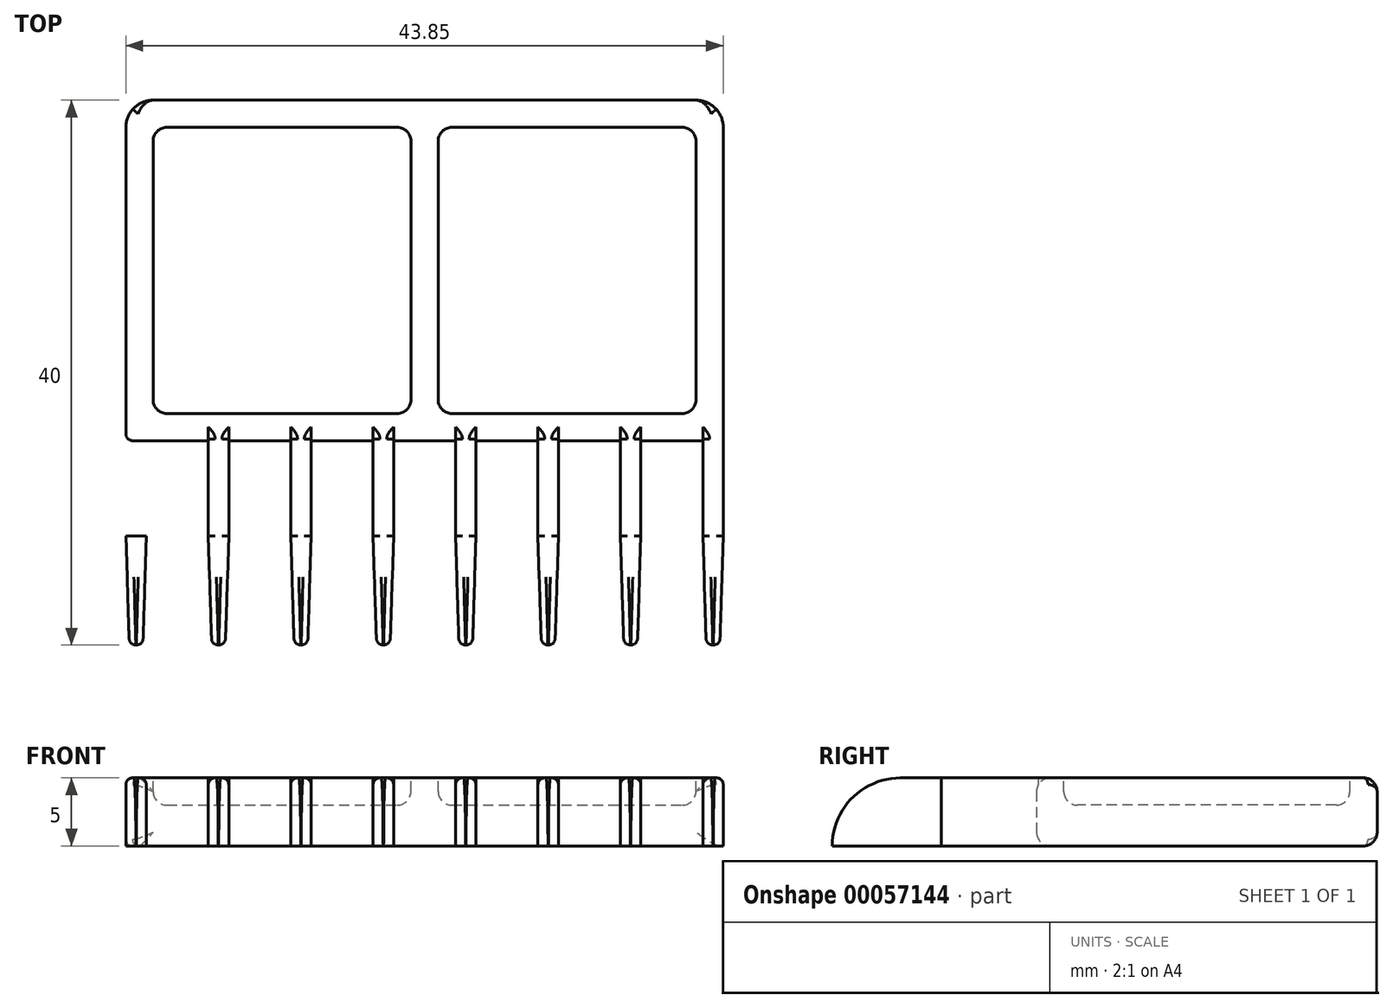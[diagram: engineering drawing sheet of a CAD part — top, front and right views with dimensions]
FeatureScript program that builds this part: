
annotation { "Feature Type Name" : "Feature", "Feature Type Description" : "" }
export const myFeature = defineFeature(function(context is Context, id is Id, definition is map)
    precondition{}
    {
        {
            var Q0;
            Q0=qCreatedBy(makeId("Top.planeOp"),FACE);
            var sketch = newSketch(context, id + "F0", { "sketchPlane" : qUnion([Q0])});
            skLineSegment(sketch, "E0.bottom", {"start": v(0, 0) * mm, "end": v(43.85, 0) * mm});
            skLineSegment(sketch, "E0.top", {"start": v(0, 25) * mm, "end": v(43.85, 25) * mm});
            skLineSegment(sketch, "E0.left", {"start": v(0, 0) * mm, "end": v(0, 25) * mm});
            skLineSegment(sketch, "E0.right", {"start": v(43.85, 0) * mm, "end": v(43.85, 25) * mm});
            skLineSegment(sketch, "E1.bottom", {"start": v(0, 0) * mm, "end": v(1.5, 0) * mm});
            skLineSegment(sketch, "E1.top", {"start": v(0, -7) * mm, "end": v(1.5, -7) * mm});
            skLineSegment(sketch, "E1.left", {"start": v(0, 0) * mm, "end": v(0, -7) * mm});
            skLineSegment(sketch, "E1.right", {"start": v(1.5, 0) * mm, "end": v(1.5, -7) * mm});
            skLineSegment(sketch, "E2", {"start": v(0, -7) * mm, "end": v(0.25, -15) * mm});
            skLineSegment(sketch, "E3", {"start": v(0.25, -15) * mm, "end": v(1.25, -15) * mm});
            skLineSegment(sketch, "E4", {"start": v(1.5, -7) * mm, "end": v(1.25, -15) * mm});
            skLineSegment(sketch, "E5.1.0.0", {"start": v(6.05, 0) * mm, "end": v(6.05, -7) * mm});
            skLineSegment(sketch, "E5.1.0.1", {"start": v(7.55, 0) * mm, "end": v(7.55, -7) * mm});
            skLineSegment(sketch, "E5.1.0.2", {"start": v(6.05, -7) * mm, "end": v(6.3, -15) * mm});
            skLineSegment(sketch, "E5.1.0.3", {"start": v(7.55, -7) * mm, "end": v(7.3, -15) * mm});
            skLineSegment(sketch, "E5.1.0.4", {"start": v(6.3, -15) * mm, "end": v(7.3, -15) * mm});
            skLineSegment(sketch, "E5.1.0.5", {"start": v(6.05, 0) * mm, "end": v(7.55, 0) * mm});
            skLineSegment(sketch, "E5.1.0.6", {"start": v(6.05, -7) * mm, "end": v(7.55, -7) * mm});
            skLineSegment(sketch, "E5.2.0.0", {"start": v(12.1, 0) * mm, "end": v(12.1, -7) * mm});
            skLineSegment(sketch, "E5.2.0.1", {"start": v(13.6, 0) * mm, "end": v(13.6, -7) * mm});
            skLineSegment(sketch, "E5.2.0.2", {"start": v(12.1, -7) * mm, "end": v(12.35, -15) * mm});
            skLineSegment(sketch, "E5.2.0.3", {"start": v(13.6, -7) * mm, "end": v(13.35, -15) * mm});
            skLineSegment(sketch, "E5.2.0.4", {"start": v(12.35, -15) * mm, "end": v(13.35, -15) * mm});
            skLineSegment(sketch, "E5.2.0.5", {"start": v(12.1, 0) * mm, "end": v(13.6, 0) * mm});
            skLineSegment(sketch, "E5.2.0.6", {"start": v(12.1, -7) * mm, "end": v(13.6, -7) * mm});
            skLineSegment(sketch, "E5.3.0.0", {"start": v(18.15, 0) * mm, "end": v(18.15, -7) * mm});
            skLineSegment(sketch, "E5.3.0.1", {"start": v(19.65, 0) * mm, "end": v(19.65, -7) * mm});
            skLineSegment(sketch, "E5.3.0.2", {"start": v(18.15, -7) * mm, "end": v(18.4, -15) * mm});
            skLineSegment(sketch, "E5.3.0.3", {"start": v(19.65, -7) * mm, "end": v(19.4, -15) * mm});
            skLineSegment(sketch, "E5.3.0.4", {"start": v(18.4, -15) * mm, "end": v(19.4, -15) * mm});
            skLineSegment(sketch, "E5.3.0.5", {"start": v(18.15, 0) * mm, "end": v(19.65, 0) * mm});
            skLineSegment(sketch, "E5.3.0.6", {"start": v(18.15, -7) * mm, "end": v(19.65, -7) * mm});
            skLineSegment(sketch, "E5.4.0.0", {"start": v(24.2, 0) * mm, "end": v(24.2, -7) * mm});
            skLineSegment(sketch, "E5.4.0.1", {"start": v(25.7, 0) * mm, "end": v(25.7, -7) * mm});
            skLineSegment(sketch, "E5.4.0.2", {"start": v(24.2, -7) * mm, "end": v(24.45, -15) * mm});
            skLineSegment(sketch, "E5.4.0.3", {"start": v(25.7, -7) * mm, "end": v(25.45, -15) * mm});
            skLineSegment(sketch, "E5.4.0.4", {"start": v(24.45, -15) * mm, "end": v(25.45, -15) * mm});
            skLineSegment(sketch, "E5.4.0.5", {"start": v(24.2, 0) * mm, "end": v(25.7, 0) * mm});
            skLineSegment(sketch, "E5.4.0.6", {"start": v(24.2, -7) * mm, "end": v(25.7, -7) * mm});
            skLineSegment(sketch, "E5.5.0.0", {"start": v(30.25, 0) * mm, "end": v(30.25, -7) * mm});
            skLineSegment(sketch, "E5.5.0.1", {"start": v(31.75, 0) * mm, "end": v(31.75, -7) * mm});
            skLineSegment(sketch, "E5.5.0.2", {"start": v(30.25, -7) * mm, "end": v(30.5, -15) * mm});
            skLineSegment(sketch, "E5.5.0.3", {"start": v(31.75, -7) * mm, "end": v(31.5, -15) * mm});
            skLineSegment(sketch, "E5.5.0.4", {"start": v(30.5, -15) * mm, "end": v(31.5, -15) * mm});
            skLineSegment(sketch, "E5.5.0.5", {"start": v(30.25, 0) * mm, "end": v(31.75, 0) * mm});
            skLineSegment(sketch, "E5.5.0.6", {"start": v(30.25, -7) * mm, "end": v(31.75, -7) * mm});
            skLineSegment(sketch, "E5.6.0.0", {"start": v(36.3, 0) * mm, "end": v(36.3, -7) * mm});
            skLineSegment(sketch, "E5.6.0.1", {"start": v(37.8, 0) * mm, "end": v(37.8, -7) * mm});
            skLineSegment(sketch, "E5.6.0.2", {"start": v(36.3, -7) * mm, "end": v(36.55, -15) * mm});
            skLineSegment(sketch, "E5.6.0.3", {"start": v(37.8, -7) * mm, "end": v(37.55, -15) * mm});
            skLineSegment(sketch, "E5.6.0.4", {"start": v(36.55, -15) * mm, "end": v(37.55, -15) * mm});
            skLineSegment(sketch, "E5.6.0.5", {"start": v(36.3, 0) * mm, "end": v(37.8, 0) * mm});
            skLineSegment(sketch, "E5.6.0.6", {"start": v(36.3, -7) * mm, "end": v(37.8, -7) * mm});
            skLineSegment(sketch, "E5.7.0.0", {"start": v(42.35, 0) * mm, "end": v(42.35, -7) * mm});
            skLineSegment(sketch, "E5.7.0.1", {"start": v(43.85, 0) * mm, "end": v(43.85, -7) * mm});
            skLineSegment(sketch, "E5.7.0.2", {"start": v(42.35, -7) * mm, "end": v(42.6, -15) * mm});
            skLineSegment(sketch, "E5.7.0.3", {"start": v(43.85, -7) * mm, "end": v(43.6, -15) * mm});
            skLineSegment(sketch, "E5.7.0.4", {"start": v(42.6, -15) * mm, "end": v(43.6, -15) * mm});
            skLineSegment(sketch, "E5.7.0.5", {"start": v(42.35, 0) * mm, "end": v(43.85, 0) * mm});
            skLineSegment(sketch, "E5.7.0.6", {"start": v(42.35, -7) * mm, "end": v(43.85, -7) * mm});
            skLineSegment(sketch, "E5.direction1", {"start": v(0, -7) * mm, "end": v(6.05, -7) * mm, "construction": true});
            skSolve(sketch);
        }
        {
            var Q0;
            Q0=makeQuery(id+"F0.imprint","IMPRINT",FACE,{"disambiguationData":[TD([[makeQuery(id+"F0.imprint","IMPRINT",EDGE,{"derivedFrom":sQuery(id+"F0.wireOp",EDGE,"E0.top")}),-1.0]])]});
            var Q1;
            Q1=makeQuery(id+"F0.imprint","IMPRINT",FACE,{"disambiguationData":[TD([[makeQuery(id+"F0.imprint","IMPRINT",EDGE,{"derivedFrom":sQuery(id+"F0.wireOp",EDGE,"E1.bottom")}),-1.0]])]});
            var Q2;
            Q2=makeQuery(id+"F0.imprint","IMPRINT",FACE,{"disambiguationData":[TD([[makeQuery(id+"F0.imprint","IMPRINT",EDGE,{"derivedFrom":sQuery(id+"F0.wireOp",EDGE,"E5.1.0.0")}),1.0]])]});
            var Q3;
            Q3=makeQuery(id+"F0.imprint","IMPRINT",FACE,{"disambiguationData":[TD([[makeQuery(id+"F0.imprint","IMPRINT",EDGE,{"derivedFrom":sQuery(id+"F0.wireOp",EDGE,"E5.2.0.0")}),1.0]])]});
            var Q4;
            Q4=makeQuery(id+"F0.imprint","IMPRINT",FACE,{"disambiguationData":[TD([[makeQuery(id+"F0.imprint","IMPRINT",EDGE,{"derivedFrom":sQuery(id+"F0.wireOp",EDGE,"E5.3.0.0")}),1.0]])]});
            var Q5;
            Q5=makeQuery(id+"F0.imprint","IMPRINT",FACE,{"disambiguationData":[TD([[makeQuery(id+"F0.imprint","IMPRINT",EDGE,{"derivedFrom":sQuery(id+"F0.wireOp",EDGE,"E5.4.0.0")}),1.0]])]});
            var Q6;
            Q6=makeQuery(id+"F0.imprint","IMPRINT",FACE,{"disambiguationData":[TD([[makeQuery(id+"F0.imprint","IMPRINT",EDGE,{"derivedFrom":sQuery(id+"F0.wireOp",EDGE,"E5.5.0.0")}),1.0]])]});
            var Q7;
            Q7=makeQuery(id+"F0.imprint","IMPRINT",FACE,{"disambiguationData":[TD([[makeQuery(id+"F0.imprint","IMPRINT",EDGE,{"derivedFrom":sQuery(id+"F0.wireOp",EDGE,"E5.6.0.0")}),1.0]])]});
            var Q8;
            Q8=makeQuery(id+"F0.imprint","IMPRINT",FACE,{"disambiguationData":[TD([[makeQuery(id+"F0.imprint","IMPRINT",EDGE,{"derivedFrom":sQuery(id+"F0.wireOp",EDGE,"E5.7.0.0")}),1.0]])]});
            var Q9;
            Q9=makeQuery(id+"F0.imprint","IMPRINT",FACE,{"disambiguationData":[TD([[makeQuery(id+"F0.imprint","IMPRINT",EDGE,{"derivedFrom":sQuery(id+"F0.wireOp",EDGE,"E1.top")}),-1.0]])]});
            var Q10;
            Q10=makeQuery(id+"F0.imprint","IMPRINT",FACE,{"disambiguationData":[TD([[makeQuery(id+"F0.imprint","IMPRINT",EDGE,{"derivedFrom":sQuery(id+"F0.wireOp",EDGE,"E5.2.0.2")}),1.0]])]});
            var Q11;
            Q11=makeQuery(id+"F0.imprint","IMPRINT",FACE,{"disambiguationData":[TD([[makeQuery(id+"F0.imprint","IMPRINT",EDGE,{"derivedFrom":sQuery(id+"F0.wireOp",EDGE,"E5.6.0.2")}),1.0]])]});
            var Q12;
            Q12=makeQuery(id+"F0.imprint","IMPRINT",FACE,{"disambiguationData":[TD([[makeQuery(id+"F0.imprint","IMPRINT",EDGE,{"derivedFrom":sQuery(id+"F0.wireOp",EDGE,"E5.4.0.2")}),1.0]])]});
            var Q13;
            Q13=makeQuery(id+"F0.imprint","IMPRINT",FACE,{"disambiguationData":[TD([[makeQuery(id+"F0.imprint","IMPRINT",EDGE,{"derivedFrom":sQuery(id+"F0.wireOp",EDGE,"E5.5.0.2")}),1.0]])]});
            var Q14;
            Q14=makeQuery(id+"F0.imprint","IMPRINT",FACE,{"disambiguationData":[TD([[makeQuery(id+"F0.imprint","IMPRINT",EDGE,{"derivedFrom":sQuery(id+"F0.wireOp",EDGE,"E5.7.0.2")}),1.0]])]});
            var Q15;
            Q15=makeQuery(id+"F0.imprint","IMPRINT",FACE,{"disambiguationData":[TD([[makeQuery(id+"F0.imprint","IMPRINT",EDGE,{"derivedFrom":sQuery(id+"F0.wireOp",EDGE,"E5.1.0.2")}),1.0]])]});
            var Q16;
            Q16=makeQuery(id+"F0.imprint","IMPRINT",FACE,{"disambiguationData":[TD([[makeQuery(id+"F0.imprint","IMPRINT",EDGE,{"derivedFrom":sQuery(id+"F0.wireOp",EDGE,"E5.3.0.2")}),1.0]])]});
            extrude(context, id + "F1", {"entities" : qUnion([Q0, Q1, Q2, Q3, Q4, Q5, Q6, Q7, Q8, Q9, Q10, Q11, Q12, Q13, Q14, Q15, Q16]), "depth" : 5 * mm});
        }
        {
            var Q0;
            Q0=makeQuery(id+"F1.opExtrude","CAP_FACE",FACE,{"disambiguationData":[OSD([sQuery(id+"F0.wireOp",EDGE,"E0.bottom"),sQuery(id+"F0.wireOp",EDGE,"E0.top"),sQuery(id+"F0.wireOp",EDGE,"E0.left"),sQuery(id+"F0.wireOp",EDGE,"E0.right"),sQuery(id+"F0.wireOp",EDGE,"e04acd4f-041c-4751-82c0-863ba9d036c2.top"),sQuery(id+"F0.wireOp",EDGE,"e04acd4f-041c-4751-82c0-863ba9d036c2.left"),sQuery(id+"F0.wireOp",EDGE,"e04acd4f-041c-4751-82c0-863ba9d036c2.right"),sQuery(id+"F0.wireOp",EDGE,"287f4ce8-5867-4a98-aaa3-2ab63182d6cb.1.0.0"),sQuery(id+"F0.wireOp",EDGE,"287f4ce8-5867-4a98-aaa3-2ab63182d6cb.1.0.2"),sQuery(id+"F0.wireOp",EDGE,"287f4ce8-5867-4a98-aaa3-2ab63182d6cb.1.0.3"),sQuery(id+"F0.wireOp",EDGE,"287f4ce8-5867-4a98-aaa3-2ab63182d6cb.2.0.0"),sQuery(id+"F0.wireOp",EDGE,"287f4ce8-5867-4a98-aaa3-2ab63182d6cb.2.0.2"),sQuery(id+"F0.wireOp",EDGE,"287f4ce8-5867-4a98-aaa3-2ab63182d6cb.2.0.3"),sQuery(id+"F0.wireOp",EDGE,"287f4ce8-5867-4a98-aaa3-2ab63182d6cb.3.0.0"),sQuery(id+"F0.wireOp",EDGE,"287f4ce8-5867-4a98-aaa3-2ab63182d6cb.3.0.2"),sQuery(id+"F0.wireOp",EDGE,"287f4ce8-5867-4a98-aaa3-2ab63182d6cb.3.0.3"),sQuery(id+"F0.wireOp",EDGE,"287f4ce8-5867-4a98-aaa3-2ab63182d6cb.4.0.0"),sQuery(id+"F0.wireOp",EDGE,"287f4ce8-5867-4a98-aaa3-2ab63182d6cb.4.0.2"),sQuery(id+"F0.wireOp",EDGE,"287f4ce8-5867-4a98-aaa3-2ab63182d6cb.4.0.3"),sQuery(id+"F0.wireOp",EDGE,"287f4ce8-5867-4a98-aaa3-2ab63182d6cb.5.0.0"),sQuery(id+"F0.wireOp",EDGE,"287f4ce8-5867-4a98-aaa3-2ab63182d6cb.5.0.2"),sQuery(id+"F0.wireOp",EDGE,"287f4ce8-5867-4a98-aaa3-2ab63182d6cb.5.0.3"),sQuery(id+"F0.wireOp",EDGE,"287f4ce8-5867-4a98-aaa3-2ab63182d6cb.6.0.0"),sQuery(id+"F0.wireOp",EDGE,"287f4ce8-5867-4a98-aaa3-2ab63182d6cb.6.0.2"),sQuery(id+"F0.wireOp",EDGE,"287f4ce8-5867-4a98-aaa3-2ab63182d6cb.6.0.3"),sQuery(id+"F0.wireOp",EDGE,"287f4ce8-5867-4a98-aaa3-2ab63182d6cb.7.0.0"),sQuery(id+"F0.wireOp",EDGE,"287f4ce8-5867-4a98-aaa3-2ab63182d6cb.7.0.2"),sQuery(id+"F0.wireOp",EDGE,"287f4ce8-5867-4a98-aaa3-2ab63182d6cb.7.0.3")])],"isStart":false});
            var sketch = newSketch(context, id + "F2", { "sketchPlane" : qUnion([Q0])});
            skLineSegment(sketch, "E6.bottom", {"start": v(2, 2) * mm, "end": v(20.92, 2) * mm});
            skLineSegment(sketch, "E6.top", {"start": v(2, 23) * mm, "end": v(20.92, 23) * mm});
            skLineSegment(sketch, "E6.left", {"start": v(2, 23) * mm, "end": v(2, 2) * mm});
            skLineSegment(sketch, "E6.right", {"start": v(20.92, 23) * mm, "end": v(20.92, 2) * mm});
            skLineSegment(sketch, "E7.bottom", {"start": v(22.92, 23) * mm, "end": v(41.85, 23) * mm});
            skLineSegment(sketch, "E7.top", {"start": v(22.92, 2) * mm, "end": v(41.85, 2) * mm});
            skLineSegment(sketch, "E7.left", {"start": v(22.92, 23) * mm, "end": v(22.92, 2) * mm});
            skLineSegment(sketch, "E7.right", {"start": v(41.85, 23) * mm, "end": v(41.85, 2) * mm});
            skSolve(sketch);
        }
        {
            var Q0;
            Q0=makeQuery(id+"F2.imprint","IMPRINT",FACE,{"disambiguationData":[TD([[makeQuery(id+"F2.imprint","IMPRINT",EDGE,{"derivedFrom":sQuery(id+"F2.wireOp",EDGE,"E6.bottom")}),1.0]])]});
            var Q1;
            Q1=makeQuery(id+"F2.imprint","IMPRINT",FACE,{"disambiguationData":[TD([[makeQuery(id+"F2.imprint","IMPRINT",EDGE,{"derivedFrom":sQuery(id+"F2.wireOp",EDGE,"E7.bottom")}),-1.0]])]});
            extrude(context, id + "F3", {"entities" : qUnion([Q0, Q1]), "operationType" : NewBodyOperationType.REMOVE, "oppositeDirection" : true, "depth" : 2 * mm});
        }
        {
            var Q0;
            Q0=makeQuery(id+"F1.opExtrude","CAP_EDGE",EDGE,{"disambiguationData":[OSD([sQuery(id+"F0.wireOp",EDGE,"E5.5.0.4")])],"isStart":false});
            var Q1;
            Q1=makeQuery(id+"F1.opExtrude","CAP_EDGE",EDGE,{"disambiguationData":[OSD([sQuery(id+"F0.wireOp",EDGE,"E5.6.0.4")])],"isStart":false});
            var Q2;
            Q2=makeQuery(id+"F1.opExtrude","CAP_EDGE",EDGE,{"disambiguationData":[OSD([sQuery(id+"F0.wireOp",EDGE,"E5.1.0.4")])],"isStart":false});
            var Q3;
            Q3=makeQuery(id+"F1.opExtrude","CAP_EDGE",EDGE,{"disambiguationData":[OSD([sQuery(id+"F0.wireOp",EDGE,"E3")])],"isStart":false});
            var Q4;
            Q4=makeQuery(id+"F1.opExtrude","CAP_EDGE",EDGE,{"disambiguationData":[OSD([sQuery(id+"F0.wireOp",EDGE,"E5.3.0.4")])],"isStart":false});
            var Q5;
            Q5=makeQuery(id+"F1.opExtrude","CAP_EDGE",EDGE,{"disambiguationData":[OSD([sQuery(id+"F0.wireOp",EDGE,"E5.2.0.4")])],"isStart":false});
            var Q6;
            Q6=makeQuery(id+"F1.opExtrude","CAP_EDGE",EDGE,{"disambiguationData":[OSD([sQuery(id+"F0.wireOp",EDGE,"E5.7.0.4")])],"isStart":false});
            var Q7;
            Q7=makeQuery(id+"F1.opExtrude","CAP_EDGE",EDGE,{"disambiguationData":[OSD([sQuery(id+"F0.wireOp",EDGE,"E5.4.0.4")])],"isStart":false});
            fillet(context, id + "F4", {"entities" : qUnion([Q0, Q1, Q2, Q3, Q4, Q5, Q6, Q7]), "radius" : 5 * mm, "tangentPropagation" : true, "allowEdgeOverflow" : false});
        }
        {
            var Q0;
            Q0=makeQuery(id+"F3.boolean.opBoolean","COPY",FACE,{"derivedFrom":makeQuery(id+"F3.opExtrude","CAP_FACE",FACE,{"disambiguationData":[OSD([sQuery(id+"F2.wireOp",EDGE,"E6.bottom"),sQuery(id+"F2.wireOp",EDGE,"E6.top"),sQuery(id+"F2.wireOp",EDGE,"E6.left"),sQuery(id+"F2.wireOp",EDGE,"E6.right")])],"isStart":false})});
            var Q1;
            Q1=makeQuery(id+"F3.boolean.opBoolean","COPY",FACE,{"derivedFrom":makeQuery(id+"F3.opExtrude","CAP_FACE",FACE,{"disambiguationData":[OSD([sQuery(id+"F2.wireOp",EDGE,"E7.bottom"),sQuery(id+"F2.wireOp",EDGE,"E7.top"),sQuery(id+"F2.wireOp",EDGE,"E7.left"),sQuery(id+"F2.wireOp",EDGE,"E7.right")])],"isStart":false})});
            var Q2;
            Q2=makeQuery(id+"F3.boolean.opBoolean","COPY",EDGE,{"derivedFrom":makeQuery(id+"F3.opExtrude","SWEPT_EDGE",EDGE,{"disambiguationData":[OSD([sQuery(id+"F2.wireOp",EDGE,"E7.bottom"),sQuery(id+"F2.wireOp",EDGE,"E7.right")])]})});
            var Q3;
            Q3=makeQuery(id+"F3.boolean.opBoolean","COPY",EDGE,{"derivedFrom":makeQuery(id+"F3.opExtrude","SWEPT_EDGE",EDGE,{"disambiguationData":[OSD([sQuery(id+"F2.wireOp",EDGE,"E6.top"),sQuery(id+"F2.wireOp",EDGE,"E6.right")])]})});
            var Q4;
            Q4=makeQuery(id+"F3.boolean.opBoolean","COPY",EDGE,{"derivedFrom":makeQuery(id+"F3.opExtrude","SWEPT_EDGE",EDGE,{"disambiguationData":[OSD([sQuery(id+"F2.wireOp",EDGE,"E6.top"),sQuery(id+"F2.wireOp",EDGE,"E6.left")])]})});
            var Q5;
            Q5=makeQuery(id+"F3.boolean.opBoolean","COPY",EDGE,{"derivedFrom":makeQuery(id+"F3.opExtrude","SWEPT_EDGE",EDGE,{"disambiguationData":[OSD([sQuery(id+"F2.wireOp",EDGE,"E7.bottom"),sQuery(id+"F2.wireOp",EDGE,"E7.left")])]})});
            var Q6;
            Q6=makeQuery(id+"F3.boolean.opBoolean","COPY",EDGE,{"derivedFrom":makeQuery(id+"F3.opExtrude","SWEPT_EDGE",EDGE,{"disambiguationData":[OSD([sQuery(id+"F2.wireOp",EDGE,"E7.top"),sQuery(id+"F2.wireOp",EDGE,"E7.right")])]})});
            var Q7;
            Q7=makeQuery(id+"F3.boolean.opBoolean","COPY",EDGE,{"derivedFrom":makeQuery(id+"F3.opExtrude","SWEPT_EDGE",EDGE,{"disambiguationData":[OSD([sQuery(id+"F2.wireOp",EDGE,"E6.bottom"),sQuery(id+"F2.wireOp",EDGE,"E6.right")])]})});
            var Q8;
            Q8=makeQuery(id+"F3.boolean.opBoolean","COPY",EDGE,{"derivedFrom":makeQuery(id+"F3.opExtrude","SWEPT_EDGE",EDGE,{"disambiguationData":[OSD([sQuery(id+"F2.wireOp",EDGE,"E7.top"),sQuery(id+"F2.wireOp",EDGE,"E7.left")])]})});
            var Q9;
            Q9=makeQuery(id+"F3.boolean.opBoolean","COPY",EDGE,{"derivedFrom":makeQuery(id+"F3.opExtrude","SWEPT_EDGE",EDGE,{"disambiguationData":[OSD([sQuery(id+"F2.wireOp",EDGE,"E6.bottom"),sQuery(id+"F2.wireOp",EDGE,"E6.left")])]})});
            var Q10;
            {var subQ0=sQuery(id+"F0.wireOp",EDGE,"E0.bottom");Q10=makeQuery(id+"F1.opExtrude","CAP_EDGE",EDGE,{"disambiguationData":[OSD([subQ0]),TDD([makeQuery(id+"F0.imprint","IMPRINT",EDGE,{"disambiguationData":[TD([[makeQuery(id+"F0.imprint","INTERSECT",VERTEX,{"derivedFrom":[subQ0,sQuery(id+"F0.wireOp",EDGE,"e04acd4f-041c-4751-82c0-863ba9d036c2.bottom"),sQuery(id+"F0.wireOp",EDGE,"e04acd4f-041c-4751-82c0-863ba9d036c2.right")]}),-1.0]])],"derivedFrom":subQ0})])],"isStart":false});}
            var Q11;
            {var subQ0=sQuery(id+"F0.wireOp",EDGE,"E0.bottom");Q11=makeQuery(id+"F1.opExtrude","CAP_EDGE",EDGE,{"disambiguationData":[OSD([subQ0]),TDD([makeQuery(id+"F0.imprint","IMPRINT",EDGE,{"disambiguationData":[TD([[makeQuery(id+"F0.imprint","INTERSECT",VERTEX,{"derivedFrom":[subQ0,sQuery(id+"F0.wireOp",EDGE,"287f4ce8-5867-4a98-aaa3-2ab63182d6cb.1.0.1"),sQuery(id+"F0.wireOp",EDGE,"287f4ce8-5867-4a98-aaa3-2ab63182d6cb.1.0.3")]}),-1.0]])],"derivedFrom":subQ0})])],"isStart":false});}
            var Q12;
            {var subQ0=sQuery(id+"F0.wireOp",EDGE,"E0.bottom");Q12=makeQuery(id+"F1.opExtrude","CAP_EDGE",EDGE,{"disambiguationData":[OSD([subQ0]),TDD([makeQuery(id+"F0.imprint","IMPRINT",EDGE,{"disambiguationData":[TD([[makeQuery(id+"F0.imprint","INTERSECT",VERTEX,{"derivedFrom":[subQ0,sQuery(id+"F0.wireOp",EDGE,"287f4ce8-5867-4a98-aaa3-2ab63182d6cb.2.0.1"),sQuery(id+"F0.wireOp",EDGE,"287f4ce8-5867-4a98-aaa3-2ab63182d6cb.2.0.3")]}),-1.0]])],"derivedFrom":subQ0})])],"isStart":false});}
            var Q13;
            {var subQ0=sQuery(id+"F0.wireOp",EDGE,"E0.bottom");Q13=makeQuery(id+"F1.opExtrude","CAP_EDGE",EDGE,{"disambiguationData":[OSD([subQ0]),TDD([makeQuery(id+"F0.imprint","IMPRINT",EDGE,{"disambiguationData":[TD([[makeQuery(id+"F0.imprint","INTERSECT",VERTEX,{"derivedFrom":[subQ0,sQuery(id+"F0.wireOp",EDGE,"287f4ce8-5867-4a98-aaa3-2ab63182d6cb.3.0.1"),sQuery(id+"F0.wireOp",EDGE,"287f4ce8-5867-4a98-aaa3-2ab63182d6cb.3.0.3")]}),-1.0]])],"derivedFrom":subQ0})])],"isStart":false});}
            var Q14;
            {var subQ0=sQuery(id+"F0.wireOp",EDGE,"E0.bottom");Q14=makeQuery(id+"F1.opExtrude","CAP_EDGE",EDGE,{"disambiguationData":[OSD([subQ0]),TDD([makeQuery(id+"F0.imprint","IMPRINT",EDGE,{"disambiguationData":[TD([[makeQuery(id+"F0.imprint","INTERSECT",VERTEX,{"derivedFrom":[subQ0,sQuery(id+"F0.wireOp",EDGE,"287f4ce8-5867-4a98-aaa3-2ab63182d6cb.4.0.1"),sQuery(id+"F0.wireOp",EDGE,"287f4ce8-5867-4a98-aaa3-2ab63182d6cb.4.0.3")]}),-1.0]])],"derivedFrom":subQ0})])],"isStart":false});}
            var Q15;
            {var subQ0=sQuery(id+"F0.wireOp",EDGE,"E0.bottom");Q15=makeQuery(id+"F1.opExtrude","CAP_EDGE",EDGE,{"disambiguationData":[OSD([subQ0]),TDD([makeQuery(id+"F0.imprint","IMPRINT",EDGE,{"disambiguationData":[TD([[makeQuery(id+"F0.imprint","INTERSECT",VERTEX,{"derivedFrom":[subQ0,sQuery(id+"F0.wireOp",EDGE,"287f4ce8-5867-4a98-aaa3-2ab63182d6cb.5.0.1"),sQuery(id+"F0.wireOp",EDGE,"287f4ce8-5867-4a98-aaa3-2ab63182d6cb.5.0.3")]}),-1.0]])],"derivedFrom":subQ0})])],"isStart":false});}
            var Q16;
            {var subQ0=sQuery(id+"F0.wireOp",EDGE,"E0.bottom");Q16=makeQuery(id+"F1.opExtrude","CAP_EDGE",EDGE,{"disambiguationData":[OSD([subQ0]),TDD([makeQuery(id+"F0.imprint","IMPRINT",EDGE,{"disambiguationData":[TD([[makeQuery(id+"F0.imprint","INTERSECT",VERTEX,{"derivedFrom":[subQ0,sQuery(id+"F0.wireOp",EDGE,"287f4ce8-5867-4a98-aaa3-2ab63182d6cb.7.0.1"),sQuery(id+"F0.wireOp",EDGE,"287f4ce8-5867-4a98-aaa3-2ab63182d6cb.7.0.2")]}),1.0]])],"derivedFrom":subQ0})])],"isStart":false});}
            var Q17;
            Q17=makeQuery(id+"F3.boolean.opBoolean","COPY",EDGE,{"derivedFrom":makeQuery(id+"F3.opExtrude","CAP_EDGE",EDGE,{"disambiguationData":[OSD([sQuery(id+"F2.wireOp",EDGE,"E6.right")])],"isStart":true})});
            var Q18;
            Q18=makeQuery(id+"F3.boolean.opBoolean","COPY",EDGE,{"derivedFrom":makeQuery(id+"F3.opExtrude","CAP_EDGE",EDGE,{"disambiguationData":[OSD([sQuery(id+"F2.wireOp",EDGE,"E7.left")])],"isStart":true})});
            var Q19;
            Q19=makeQuery(id+"F1.opExtrude","CAP_EDGE",EDGE,{"disambiguationData":[OSD([sQuery(id+"F0.wireOp",EDGE,"E0.top")])],"isStart":false});
            var Q20;
            Q20=makeQuery(id+"F1.opExtrude","CAP_EDGE",EDGE,{"disambiguationData":[OSD([sQuery(id+"F0.wireOp",EDGE,"E0.top")])],"isStart":true});
            var Q21;
            {var subQ0=sQuery(id+"F0.wireOp",EDGE,"E0.bottom");Q21=makeQuery(id+"F1.opExtrude","CAP_EDGE",EDGE,{"disambiguationData":[OSD([subQ0]),TDD([makeQuery(id+"F0.imprint","IMPRINT",EDGE,{"disambiguationData":[TD([[makeQuery(id+"F0.imprint","INTERSECT",VERTEX,{"derivedFrom":[subQ0,sQuery(id+"F0.wireOp",EDGE,"e04acd4f-041c-4751-82c0-863ba9d036c2.bottom"),sQuery(id+"F0.wireOp",EDGE,"e04acd4f-041c-4751-82c0-863ba9d036c2.right")]}),-1.0]])],"derivedFrom":subQ0})])],"isStart":true});}
            var Q22;
            {var subQ0=sQuery(id+"F0.wireOp",EDGE,"E0.bottom");Q22=makeQuery(id+"F1.opExtrude","CAP_EDGE",EDGE,{"disambiguationData":[OSD([subQ0]),TDD([makeQuery(id+"F0.imprint","IMPRINT",EDGE,{"disambiguationData":[TD([[makeQuery(id+"F0.imprint","INTERSECT",VERTEX,{"derivedFrom":[subQ0,sQuery(id+"F0.wireOp",EDGE,"287f4ce8-5867-4a98-aaa3-2ab63182d6cb.1.0.1"),sQuery(id+"F0.wireOp",EDGE,"287f4ce8-5867-4a98-aaa3-2ab63182d6cb.1.0.3")]}),-1.0]])],"derivedFrom":subQ0})])],"isStart":true});}
            var Q23;
            {var subQ0=sQuery(id+"F0.wireOp",EDGE,"E0.bottom");Q23=makeQuery(id+"F1.opExtrude","CAP_EDGE",EDGE,{"disambiguationData":[OSD([subQ0]),TDD([makeQuery(id+"F0.imprint","IMPRINT",EDGE,{"disambiguationData":[TD([[makeQuery(id+"F0.imprint","INTERSECT",VERTEX,{"derivedFrom":[subQ0,sQuery(id+"F0.wireOp",EDGE,"287f4ce8-5867-4a98-aaa3-2ab63182d6cb.2.0.1"),sQuery(id+"F0.wireOp",EDGE,"287f4ce8-5867-4a98-aaa3-2ab63182d6cb.2.0.3")]}),-1.0]])],"derivedFrom":subQ0})])],"isStart":true});}
            var Q24;
            {var subQ0=sQuery(id+"F0.wireOp",EDGE,"E0.bottom");Q24=makeQuery(id+"F1.opExtrude","CAP_EDGE",EDGE,{"disambiguationData":[OSD([subQ0]),TDD([makeQuery(id+"F0.imprint","IMPRINT",EDGE,{"disambiguationData":[TD([[makeQuery(id+"F0.imprint","INTERSECT",VERTEX,{"derivedFrom":[subQ0,sQuery(id+"F0.wireOp",EDGE,"287f4ce8-5867-4a98-aaa3-2ab63182d6cb.3.0.1"),sQuery(id+"F0.wireOp",EDGE,"287f4ce8-5867-4a98-aaa3-2ab63182d6cb.3.0.3")]}),-1.0]])],"derivedFrom":subQ0})])],"isStart":true});}
            var Q25;
            {var subQ0=sQuery(id+"F0.wireOp",EDGE,"E0.bottom");Q25=makeQuery(id+"F1.opExtrude","CAP_EDGE",EDGE,{"disambiguationData":[OSD([subQ0]),TDD([makeQuery(id+"F0.imprint","IMPRINT",EDGE,{"disambiguationData":[TD([[makeQuery(id+"F0.imprint","INTERSECT",VERTEX,{"derivedFrom":[subQ0,sQuery(id+"F0.wireOp",EDGE,"287f4ce8-5867-4a98-aaa3-2ab63182d6cb.4.0.1"),sQuery(id+"F0.wireOp",EDGE,"287f4ce8-5867-4a98-aaa3-2ab63182d6cb.4.0.3")]}),-1.0]])],"derivedFrom":subQ0})])],"isStart":true});}
            var Q26;
            {var subQ0=sQuery(id+"F0.wireOp",EDGE,"E0.bottom");Q26=makeQuery(id+"F1.opExtrude","CAP_EDGE",EDGE,{"disambiguationData":[OSD([subQ0]),TDD([makeQuery(id+"F0.imprint","IMPRINT",EDGE,{"disambiguationData":[TD([[makeQuery(id+"F0.imprint","INTERSECT",VERTEX,{"derivedFrom":[subQ0,sQuery(id+"F0.wireOp",EDGE,"287f4ce8-5867-4a98-aaa3-2ab63182d6cb.5.0.1"),sQuery(id+"F0.wireOp",EDGE,"287f4ce8-5867-4a98-aaa3-2ab63182d6cb.5.0.3")]}),-1.0]])],"derivedFrom":subQ0})])],"isStart":true});}
            var Q27;
            {var subQ0=sQuery(id+"F0.wireOp",EDGE,"E0.bottom");Q27=makeQuery(id+"F1.opExtrude","CAP_EDGE",EDGE,{"disambiguationData":[OSD([subQ0]),TDD([makeQuery(id+"F0.imprint","IMPRINT",EDGE,{"disambiguationData":[TD([[makeQuery(id+"F0.imprint","INTERSECT",VERTEX,{"derivedFrom":[subQ0,sQuery(id+"F0.wireOp",EDGE,"287f4ce8-5867-4a98-aaa3-2ab63182d6cb.7.0.1"),sQuery(id+"F0.wireOp",EDGE,"287f4ce8-5867-4a98-aaa3-2ab63182d6cb.7.0.2")]}),1.0]])],"derivedFrom":subQ0})])],"isStart":true});}
            fillet(context, id + "F5", {"entities" : qUnion([Q0, Q1, Q2, Q3, Q4, Q5, Q6, Q7, Q8, Q9, Q10, Q11, Q12, Q13, Q14, Q15, Q16, Q17, Q18, Q19, Q20, Q21, Q22, Q23, Q24, Q25, Q26, Q27]), "radius" : 1 * mm, "tangentPropagation" : true, "allowEdgeOverflow" : false});
        }
        {
            var Q0;
            Q0=makeQuery(id+"F1.opExtrude","SWEPT_EDGE",EDGE,{"disambiguationData":[OSD([sQuery(id+"F0.wireOp",EDGE,"E0.top"),sQuery(id+"F0.wireOp",EDGE,"E0.left")])]});
            var Q1;
            Q1=makeQuery(id+"F1.opExtrude","SWEPT_EDGE",EDGE,{"disambiguationData":[OSD([sQuery(id+"F0.wireOp",EDGE,"E0.top"),sQuery(id+"F0.wireOp",EDGE,"E0.right")])]});
            fillet(context, id + "F6", {"entities" : qUnion([Q0, Q1]), "radius" : 2 * mm, "allowEdgeOverflow" : false});
        }
        {
            var Q0;
            Q0=makeQuery(id+"F1.opExtrude","CAP_EDGE",EDGE,{"disambiguationData":[OSD([sQuery(id+"F0.wireOp",EDGE,"E0.left"),sQuery(id+"F0.wireOp",EDGE,"E1.left")])],"isStart":false});
            var Q1;
            Q1=makeQuery(id+"F1.opExtrude","CAP_EDGE",EDGE,{"disambiguationData":[OSD([sQuery(id+"F0.wireOp",EDGE,"E1.right")])],"isStart":false});
            var Q2;
            Q2=makeQuery(id+"F1.opExtrude","CAP_EDGE",EDGE,{"disambiguationData":[OSD([sQuery(id+"F0.wireOp",EDGE,"E2")])],"isStart":false});
            var Q3;
            Q3=makeQuery(id+"F4.opFillet","BLEND_EDGE",EDGE,{"blendedFrom":[makeQuery(id+"F1.opExtrude","CAP_EDGE",EDGE,{"disambiguationData":[OSD([sQuery(id+"F0.wireOp",EDGE,"E3")])],"isStart":false}),makeQuery(id+"F1.opExtrude","SWEPT_FACE",FACE,{"disambiguationData":[OSD([sQuery(id+"F0.wireOp",EDGE,"E2")])]})],"blendedInto":[makeQuery(id+"F1.opExtrude","SWEPT_FACE",FACE,{"disambiguationData":[OSD([sQuery(id+"F0.wireOp",EDGE,"E2")])]})]});
            var Q4;
            Q4=makeQuery(id+"F1.opExtrude","CAP_EDGE",EDGE,{"disambiguationData":[OSD([sQuery(id+"F0.wireOp",EDGE,"E4")])],"isStart":false});
            var Q5;
            Q5=makeQuery(id+"F1.opExtrude","CAP_EDGE",EDGE,{"disambiguationData":[OSD([sQuery(id+"F0.wireOp",EDGE,"E5.1.0.0")])],"isStart":false});
            var Q6;
            Q6=makeQuery(id+"F1.opExtrude","CAP_EDGE",EDGE,{"disambiguationData":[OSD([sQuery(id+"F0.wireOp",EDGE,"E5.1.0.2")])],"isStart":false});
            var Q7;
            Q7=makeQuery(id+"F1.opExtrude","CAP_EDGE",EDGE,{"disambiguationData":[OSD([sQuery(id+"F0.wireOp",EDGE,"E5.1.0.1")])],"isStart":false});
            var Q8;
            Q8=makeQuery(id+"F1.opExtrude","CAP_EDGE",EDGE,{"disambiguationData":[OSD([sQuery(id+"F0.wireOp",EDGE,"E5.1.0.3")])],"isStart":false});
            var Q9;
            Q9=makeQuery(id+"F1.opExtrude","CAP_EDGE",EDGE,{"disambiguationData":[OSD([sQuery(id+"F0.wireOp",EDGE,"E5.2.0.0")])],"isStart":false});
            var Q10;
            Q10=makeQuery(id+"F1.opExtrude","CAP_EDGE",EDGE,{"disambiguationData":[OSD([sQuery(id+"F0.wireOp",EDGE,"E5.2.0.2")])],"isStart":false});
            var Q11;
            Q11=makeQuery(id+"F1.opExtrude","CAP_EDGE",EDGE,{"disambiguationData":[OSD([sQuery(id+"F0.wireOp",EDGE,"E5.2.0.1")])],"isStart":false});
            var Q12;
            Q12=makeQuery(id+"F1.opExtrude","CAP_EDGE",EDGE,{"disambiguationData":[OSD([sQuery(id+"F0.wireOp",EDGE,"E5.2.0.3")])],"isStart":false});
            var Q13;
            Q13=makeQuery(id+"F1.opExtrude","CAP_EDGE",EDGE,{"disambiguationData":[OSD([sQuery(id+"F0.wireOp",EDGE,"E5.3.0.0")])],"isStart":false});
            var Q14;
            Q14=makeQuery(id+"F1.opExtrude","CAP_EDGE",EDGE,{"disambiguationData":[OSD([sQuery(id+"F0.wireOp",EDGE,"E5.3.0.2")])],"isStart":false});
            var Q15;
            Q15=makeQuery(id+"F1.opExtrude","CAP_EDGE",EDGE,{"disambiguationData":[OSD([sQuery(id+"F0.wireOp",EDGE,"E5.3.0.1")])],"isStart":false});
            var Q16;
            Q16=makeQuery(id+"F1.opExtrude","CAP_EDGE",EDGE,{"disambiguationData":[OSD([sQuery(id+"F0.wireOp",EDGE,"E5.3.0.3")])],"isStart":false});
            var Q17;
            Q17=makeQuery(id+"F1.opExtrude","CAP_EDGE",EDGE,{"disambiguationData":[OSD([sQuery(id+"F0.wireOp",EDGE,"E5.4.0.0")])],"isStart":false});
            var Q18;
            Q18=makeQuery(id+"F1.opExtrude","CAP_EDGE",EDGE,{"disambiguationData":[OSD([sQuery(id+"F0.wireOp",EDGE,"E5.4.0.2")])],"isStart":false});
            var Q19;
            Q19=makeQuery(id+"F1.opExtrude","CAP_EDGE",EDGE,{"disambiguationData":[OSD([sQuery(id+"F0.wireOp",EDGE,"E5.4.0.1")])],"isStart":false});
            var Q20;
            Q20=makeQuery(id+"F1.opExtrude","CAP_EDGE",EDGE,{"disambiguationData":[OSD([sQuery(id+"F0.wireOp",EDGE,"E5.4.0.3")])],"isStart":false});
            var Q21;
            Q21=makeQuery(id+"F1.opExtrude","CAP_EDGE",EDGE,{"disambiguationData":[OSD([sQuery(id+"F0.wireOp",EDGE,"E5.5.0.0")])],"isStart":false});
            var Q22;
            Q22=makeQuery(id+"F1.opExtrude","CAP_EDGE",EDGE,{"disambiguationData":[OSD([sQuery(id+"F0.wireOp",EDGE,"E5.5.0.2")])],"isStart":false});
            var Q23;
            Q23=makeQuery(id+"F1.opExtrude","CAP_EDGE",EDGE,{"disambiguationData":[OSD([sQuery(id+"F0.wireOp",EDGE,"E5.5.0.1")])],"isStart":false});
            var Q24;
            Q24=makeQuery(id+"F1.opExtrude","CAP_EDGE",EDGE,{"disambiguationData":[OSD([sQuery(id+"F0.wireOp",EDGE,"E5.5.0.3")])],"isStart":false});
            var Q25;
            Q25=makeQuery(id+"F1.opExtrude","CAP_EDGE",EDGE,{"disambiguationData":[OSD([sQuery(id+"F0.wireOp",EDGE,"E5.6.0.0")])],"isStart":false});
            var Q26;
            Q26=makeQuery(id+"F1.opExtrude","CAP_EDGE",EDGE,{"disambiguationData":[OSD([sQuery(id+"F0.wireOp",EDGE,"E5.6.0.2")])],"isStart":false});
            var Q27;
            Q27=makeQuery(id+"F1.opExtrude","CAP_EDGE",EDGE,{"disambiguationData":[OSD([sQuery(id+"F0.wireOp",EDGE,"E5.6.0.1")])],"isStart":false});
            var Q28;
            Q28=makeQuery(id+"F1.opExtrude","CAP_EDGE",EDGE,{"disambiguationData":[OSD([sQuery(id+"F0.wireOp",EDGE,"E5.6.0.3")])],"isStart":false});
            var Q29;
            Q29=makeQuery(id+"F1.opExtrude","CAP_EDGE",EDGE,{"disambiguationData":[OSD([sQuery(id+"F0.wireOp",EDGE,"E5.7.0.0")])],"isStart":false});
            var Q30;
            Q30=makeQuery(id+"F1.opExtrude","CAP_EDGE",EDGE,{"disambiguationData":[OSD([sQuery(id+"F0.wireOp",EDGE,"E5.7.0.2")])],"isStart":false});
            var Q31;
            Q31=makeQuery(id+"F1.opExtrude","CAP_EDGE",EDGE,{"disambiguationData":[OSD([sQuery(id+"F0.wireOp",EDGE,"E0.right"),sQuery(id+"F0.wireOp",EDGE,"E5.7.0.1")])],"isStart":false});
            var Q32;
            Q32=makeQuery(id+"F1.opExtrude","CAP_EDGE",EDGE,{"disambiguationData":[OSD([sQuery(id+"F0.wireOp",EDGE,"E5.7.0.3")])],"isStart":false});
            fillet(context, id + "F7", {"entities" : qUnion([Q0, Q1, Q2, Q3, Q4, Q5, Q6, Q7, Q8, Q9, Q10, Q11, Q12, Q13, Q14, Q15, Q16, Q17, Q18, Q19, Q20, Q21, Q22, Q23, Q24, Q25, Q26, Q27, Q28, Q29, Q30, Q31, Q32]), "radius" : 0.5 * mm, "tangentPropagation" : true, "allowEdgeOverflow" : false});
        }
    });
